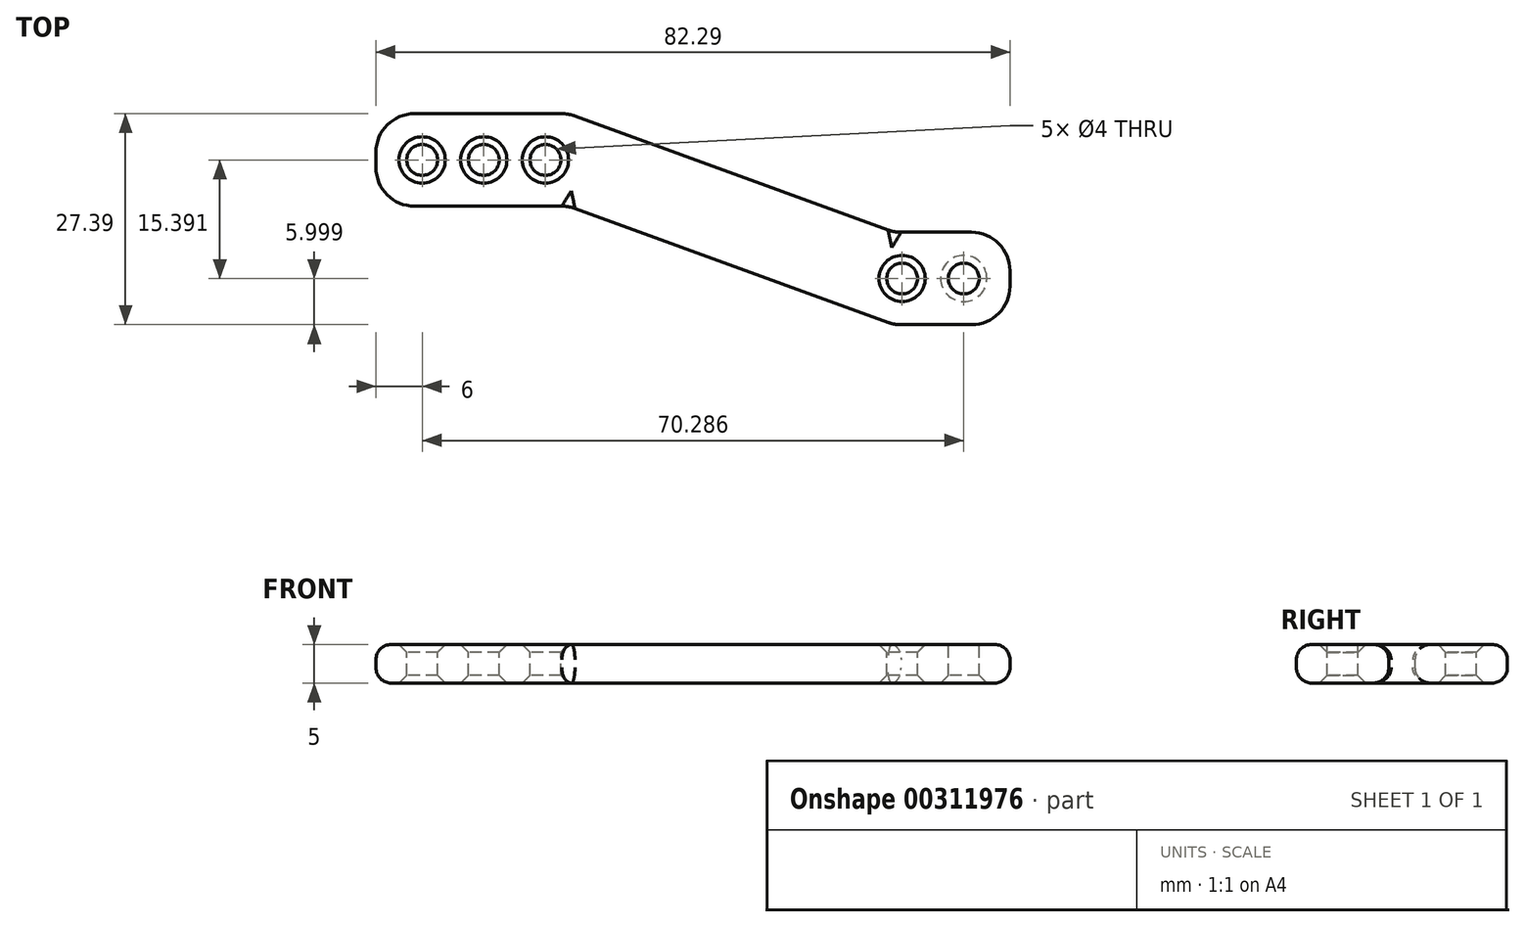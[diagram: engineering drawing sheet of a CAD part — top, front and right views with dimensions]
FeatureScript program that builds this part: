
annotation { "Feature Type Name" : "Feature", "Feature Type Description" : "" }
export const myFeature = defineFeature(function(context is Context, id is Id, definition is map)
    precondition{}
    {
        {
            var Q0;
            Q0=qCreatedBy(makeId("Top.planeOp"),FACE);
            var sketch = newSketch(context, id + "F0", { "sketchPlane" : qUnion([Q0])});
            skLineSegment(sketch, "E0.bottom", {"start": v(0, 0) * mm, "end": v(25, 0) * mm});
            skLineSegment(sketch, "E0.top", {"start": v(0, -12) * mm, "end": v(25, -12) * mm});
            skLineSegment(sketch, "E0.left", {"start": v(0, 0) * mm, "end": v(0, -12) * mm});
            skLineSegment(sketch, "E0.right", {"start": v(25, 0) * mm, "end": v(25, -12) * mm});
            skLineSegment(sketch, "E1", {"start": v(25, -12) * mm, "end": v(67.29, -27.4) * mm});
            skLineSegment(sketch, "E2.bottom", {"start": v(67.29, -27.4) * mm, "end": v(82.29, -27.4) * mm});
            skLineSegment(sketch, "E2.top", {"start": v(67.29, -15.4) * mm, "end": v(82.29, -15.4) * mm});
            skLineSegment(sketch, "E2.left", {"start": v(67.29, -27.4) * mm, "end": v(67.29, -15.4) * mm});
            skLineSegment(sketch, "E2.right", {"start": v(82.29, -27.4) * mm, "end": v(82.29, -15.4) * mm});
            skLineSegment(sketch, "E3", {"start": v(25, 0) * mm, "end": v(67.29, -15.4) * mm});
            skSolve(sketch);
        }
        {
            var Q0;
            Q0=makeQuery(id+"F0.imprint","IMPRINT",FACE,{"disambiguationData":[TD([[makeQuery(id+"F0.imprint","IMPRINT",EDGE,{"derivedFrom":sQuery(id+"F0.wireOp",EDGE,"E0.bottom")}),-1.0]])]});
            var Q1;
            Q1=makeQuery(id+"F0.imprint","IMPRINT",FACE,{"disambiguationData":[TD([[makeQuery(id+"F0.imprint","IMPRINT",EDGE,{"derivedFrom":sQuery(id+"F0.wireOp",EDGE,"E0.right")}),1.0]])]});
            var Q2;
            Q2=makeQuery(id+"F0.imprint","IMPRINT",FACE,{"disambiguationData":[TD([[makeQuery(id+"F0.imprint","IMPRINT",EDGE,{"derivedFrom":sQuery(id+"F0.wireOp",EDGE,"E2.bottom")}),1.0]])]});
            extrude(context, id + "F1", {"entities" : qUnion([Q0, Q1, Q2]), "depth" : 5 * mm});
        }
        {
            var Q0;
            Q0=makeQuery(id+"F1.opExtrude","CAP_FACE",FACE,{"disambiguationData":[OSD([sQuery(id+"F0.wireOp",EDGE,"E0.bottom"),sQuery(id+"F0.wireOp",EDGE,"E0.top"),sQuery(id+"F0.wireOp",EDGE,"E0.left"),sQuery(id+"F0.wireOp",EDGE,"E1"),sQuery(id+"F0.wireOp",EDGE,"E2.bottom"),sQuery(id+"F0.wireOp",EDGE,"E2.top"),sQuery(id+"F0.wireOp",EDGE,"E2.right"),sQuery(id+"F0.wireOp",EDGE,"E3")])],"isStart":false});
            var sketch = newSketch(context, id + "F2", { "sketchPlane" : qUnion([Q0])});
            skCircle(sketch, "E4", {"center": v(6, -6) * mm, "radius": 2 * mm});
            skCircle(sketch, "E5", {"center": v(76.29, -21.4) * mm, "radius": 2 * mm});
            skCircle(sketch, "E6.1.0.0", {"center": v(14, -6) * mm, "radius": 2 * mm});
            skCircle(sketch, "E6.2.0.0", {"center": v(22, -6) * mm, "radius": 2 * mm});
            skLineSegment(sketch, "E6.direction1", {"start": v(6, -6) * mm, "end": v(14, -6) * mm, "construction": true});
            skCircle(sketch, "E7.1.0.0", {"center": v(68.29, -21.4) * mm, "radius": 2 * mm});
            skLineSegment(sketch, "E7.direction1", {"start": v(76.29, -21.4) * mm, "end": v(68.29, -21.4) * mm, "construction": true});
            skSolve(sketch);
        }
        {
            var Q0;
            Q0 = qSketchRegion(id + "F2", true);
            extrude(context, id + "F3", {"entities" : qUnion([Q0]), "operationType" : NewBodyOperationType.REMOVE, "endBound" : BoundingType.THROUGH_ALL, "oppositeDirection" : true, "depth" : 5 * mm});
        }
        {
            var Q0;
            Q0=makeQuery(id+"F1.opExtrude","CAP_EDGE",EDGE,{"disambiguationData":[OSD([sQuery(id+"F0.wireOp",EDGE,"E0.bottom")])],"isStart":false});
            var Q1;
            Q1=makeQuery(id+"F1.opExtrude","CAP_EDGE",EDGE,{"disambiguationData":[OSD([sQuery(id+"F0.wireOp",EDGE,"E3")])],"isStart":false});
            var Q2;
            Q2=makeQuery(id+"F1.opExtrude","CAP_EDGE",EDGE,{"disambiguationData":[OSD([sQuery(id+"F0.wireOp",EDGE,"E2.top")])],"isStart":false});
            var Q3;
            Q3=makeQuery(id+"F1.opExtrude","CAP_EDGE",EDGE,{"disambiguationData":[OSD([sQuery(id+"F0.wireOp",EDGE,"E2.right")])],"isStart":false});
            var Q4;
            Q4=makeQuery(id+"F1.opExtrude","CAP_EDGE",EDGE,{"disambiguationData":[OSD([sQuery(id+"F0.wireOp",EDGE,"E2.bottom")])],"isStart":false});
            var Q5;
            Q5=makeQuery(id+"F1.opExtrude","CAP_EDGE",EDGE,{"disambiguationData":[OSD([sQuery(id+"F0.wireOp",EDGE,"E1")])],"isStart":false});
            var Q6;
            Q6=makeQuery(id+"F1.opExtrude","CAP_EDGE",EDGE,{"disambiguationData":[OSD([sQuery(id+"F0.wireOp",EDGE,"E0.top")])],"isStart":false});
            var Q7;
            Q7=makeQuery(id+"F1.opExtrude","CAP_EDGE",EDGE,{"disambiguationData":[OSD([sQuery(id+"F0.wireOp",EDGE,"E0.left")])],"isStart":false});
            fillet(context, id + "F4", {"entities" : qUnion([Q0, Q1, Q2, Q3, Q4, Q5, Q6, Q7]), "radius" : 2 * mm, "tangentPropagation" : true, "allowEdgeOverflow" : false});
        }
        {
            var Q0;
            Q0=makeQuery(id+"F1.opExtrude","CAP_EDGE",EDGE,{"disambiguationData":[OSD([sQuery(id+"F0.wireOp",EDGE,"E0.top")])],"isStart":true});
            var Q1;
            Q1=makeQuery(id+"F1.opExtrude","CAP_EDGE",EDGE,{"disambiguationData":[OSD([sQuery(id+"F0.wireOp",EDGE,"E1")])],"isStart":true});
            var Q2;
            Q2=makeQuery(id+"F1.opExtrude","CAP_EDGE",EDGE,{"disambiguationData":[OSD([sQuery(id+"F0.wireOp",EDGE,"E2.bottom")])],"isStart":true});
            var Q3;
            Q3=makeQuery(id+"F1.opExtrude","CAP_EDGE",EDGE,{"disambiguationData":[OSD([sQuery(id+"F0.wireOp",EDGE,"E2.right")])],"isStart":true});
            var Q4;
            Q4=makeQuery(id+"F1.opExtrude","CAP_EDGE",EDGE,{"disambiguationData":[OSD([sQuery(id+"F0.wireOp",EDGE,"E2.top")])],"isStart":true});
            var Q5;
            Q5=makeQuery(id+"F1.opExtrude","CAP_EDGE",EDGE,{"disambiguationData":[OSD([sQuery(id+"F0.wireOp",EDGE,"E3")])],"isStart":true});
            var Q6;
            Q6=makeQuery(id+"F1.opExtrude","CAP_EDGE",EDGE,{"disambiguationData":[OSD([sQuery(id+"F0.wireOp",EDGE,"E0.left")])],"isStart":true});
            var Q7;
            Q7=makeQuery(id+"F1.opExtrude","CAP_EDGE",EDGE,{"disambiguationData":[OSD([sQuery(id+"F0.wireOp",EDGE,"E0.bottom")])],"isStart":true});
            fillet(context, id + "F5", {"entities" : qUnion([Q0, Q1, Q2, Q3, Q4, Q5, Q6, Q7]), "radius" : 2 * mm, "tangentPropagation" : true, "allowEdgeOverflow" : false});
        }
        {
            var Q0;
            Q0=makeQuery(id+"F4.opFillet","BLEND_EDGE",EDGE,{"blendedFrom":[makeQuery(id+"F1.opExtrude","CAP_EDGE",EDGE,{"disambiguationData":[OSD([sQuery(id+"F0.wireOp",EDGE,"E0.top")])],"isStart":false}),makeQuery(id+"F1.opExtrude","CAP_EDGE",EDGE,{"disambiguationData":[OSD([sQuery(id+"F0.wireOp",EDGE,"E0.left")])],"isStart":false})],"blendedInto":[]});
            var Q1;
            Q1=makeQuery(id+"F4.opFillet","BLEND_EDGE",EDGE,{"blendedFrom":[makeQuery(id+"F1.opExtrude","CAP_EDGE",EDGE,{"disambiguationData":[OSD([sQuery(id+"F0.wireOp",EDGE,"E0.top")])],"isStart":false}),makeQuery(id+"F1.opExtrude","CAP_EDGE",EDGE,{"disambiguationData":[OSD([sQuery(id+"F0.wireOp",EDGE,"E1")])],"isStart":false})],"blendedInto":[]});
            var Q2;
            Q2=makeQuery(id+"F4.opFillet","BLEND_EDGE",EDGE,{"blendedFrom":[makeQuery(id+"F1.opExtrude","CAP_EDGE",EDGE,{"disambiguationData":[OSD([sQuery(id+"F0.wireOp",EDGE,"E1")])],"isStart":false}),makeQuery(id+"F1.opExtrude","CAP_EDGE",EDGE,{"disambiguationData":[OSD([sQuery(id+"F0.wireOp",EDGE,"E2.bottom")])],"isStart":false})],"blendedInto":[]});
            var Q3;
            Q3=makeQuery(id+"F4.opFillet","BLEND_EDGE",EDGE,{"blendedFrom":[makeQuery(id+"F1.opExtrude","CAP_EDGE",EDGE,{"disambiguationData":[OSD([sQuery(id+"F0.wireOp",EDGE,"E2.bottom")])],"isStart":false}),makeQuery(id+"F1.opExtrude","CAP_EDGE",EDGE,{"disambiguationData":[OSD([sQuery(id+"F0.wireOp",EDGE,"E2.right")])],"isStart":false})],"blendedInto":[]});
            var Q4;
            Q4=makeQuery(id+"F4.opFillet","BLEND_EDGE",EDGE,{"blendedFrom":[makeQuery(id+"F1.opExtrude","CAP_EDGE",EDGE,{"disambiguationData":[OSD([sQuery(id+"F0.wireOp",EDGE,"E2.top")])],"isStart":false}),makeQuery(id+"F1.opExtrude","CAP_EDGE",EDGE,{"disambiguationData":[OSD([sQuery(id+"F0.wireOp",EDGE,"E2.right")])],"isStart":false})],"blendedInto":[]});
            var Q5;
            Q5=makeQuery(id+"F4.opFillet","BLEND_EDGE",EDGE,{"blendedFrom":[makeQuery(id+"F1.opExtrude","CAP_EDGE",EDGE,{"disambiguationData":[OSD([sQuery(id+"F0.wireOp",EDGE,"E2.top")])],"isStart":false}),makeQuery(id+"F1.opExtrude","CAP_EDGE",EDGE,{"disambiguationData":[OSD([sQuery(id+"F0.wireOp",EDGE,"E3")])],"isStart":false})],"blendedInto":[]});
            var Q6;
            Q6=makeQuery(id+"F4.opFillet","BLEND_EDGE",EDGE,{"blendedFrom":[makeQuery(id+"F1.opExtrude","CAP_EDGE",EDGE,{"disambiguationData":[OSD([sQuery(id+"F0.wireOp",EDGE,"E0.bottom")])],"isStart":false}),makeQuery(id+"F1.opExtrude","CAP_EDGE",EDGE,{"disambiguationData":[OSD([sQuery(id+"F0.wireOp",EDGE,"E3")])],"isStart":false})],"blendedInto":[]});
            var Q7;
            Q7=makeQuery(id+"F4.opFillet","BLEND_EDGE",EDGE,{"blendedFrom":[makeQuery(id+"F1.opExtrude","CAP_EDGE",EDGE,{"disambiguationData":[OSD([sQuery(id+"F0.wireOp",EDGE,"E0.bottom")])],"isStart":false}),makeQuery(id+"F1.opExtrude","CAP_EDGE",EDGE,{"disambiguationData":[OSD([sQuery(id+"F0.wireOp",EDGE,"E0.left")])],"isStart":false})],"blendedInto":[]});
            fillet(context, id + "F6", {"entities" : qUnion([Q0, Q1, Q2, Q3, Q4, Q5, Q6, Q7]), "radius" : 5 * mm, "tangentPropagation" : true, "allowEdgeOverflow" : false});
        }
        {
            var Q0;
            Q0=makeQuery(id+"F3.boolean.opBoolean","COPY",FACE,{"derivedFrom":makeQuery(id+"F3.opExtrude","SWEPT_FACE",FACE,{"disambiguationData":[OSD([sQuery(id+"F2.wireOp",EDGE,"E4")])]})});
            var Q1;
            Q1=makeQuery(id+"F3.boolean.opBoolean","COPY",FACE,{"derivedFrom":makeQuery(id+"F3.opExtrude","SWEPT_FACE",FACE,{"disambiguationData":[OSD([sQuery(id+"F2.wireOp",EDGE,"E6.1.0.0")])]})});
            var Q2;
            Q2=makeQuery(id+"F3.boolean.opBoolean","COPY",FACE,{"derivedFrom":makeQuery(id+"F3.opExtrude","SWEPT_FACE",FACE,{"disambiguationData":[OSD([sQuery(id+"F2.wireOp",EDGE,"E6.2.0.0")])]})});
            var Q3;
            Q3=makeQuery(id+"F3.boolean.opBoolean","COPY",FACE,{"derivedFrom":makeQuery(id+"F3.opExtrude","SWEPT_FACE",FACE,{"disambiguationData":[OSD([sQuery(id+"F2.wireOp",EDGE,"E7.1.0.0")])]})});
            var Q4;
            Q4=makeQuery(id+"F3.boolean.opBoolean","COPY",EDGE,{"derivedFrom":makeQuery(id+"F3.opExtrude","CAP_EDGE",EDGE,{"disambiguationData":[OSD([sQuery(id+"F2.wireOp",EDGE,"E5")])],"isStart":true})});
            var Q5;
            Q5=makeQuery(id+"F3.boolean.opBoolean","INTERSECT",EDGE,{"derivedFrom":[makeQuery(id+"F1.opExtrude","CAP_FACE",FACE,{"disambiguationData":[OSD([sQuery(id+"F0.wireOp",EDGE,"E0.bottom"),sQuery(id+"F0.wireOp",EDGE,"E0.top"),sQuery(id+"F0.wireOp",EDGE,"E0.left"),sQuery(id+"F0.wireOp",EDGE,"E1"),sQuery(id+"F0.wireOp",EDGE,"E2.bottom"),sQuery(id+"F0.wireOp",EDGE,"E2.top"),sQuery(id+"F0.wireOp",EDGE,"E2.right"),sQuery(id+"F0.wireOp",EDGE,"E3")])],"isStart":true}),makeQuery(id+"F3.opExtrude","SWEPT_FACE",FACE,{"disambiguationData":[OSD([sQuery(id+"F2.wireOp",EDGE,"E5")])]})]});
            chamfer(context, id + "F7", {"entities" : qUnion([Q0, Q1, Q2, Q3, Q4, Q5]), "width" : 1 * mm, "tangentPropagation" : true});
        }
    });
